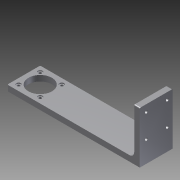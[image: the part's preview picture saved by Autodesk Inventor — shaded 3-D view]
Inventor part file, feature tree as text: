
AUTODESK INVENTOR PART (.ipt)
format: ipt  version: 2011 (Build 150239000, 239)  size: 169,984 bytes
history: native  units: mm
features: extrude x7, sketch x7, fillet x3, projected_geometry x1
ambient origin geometry x8: Origin, YZ Plane, XZ Plane, XY Plane, X Axis, Y Axis, Z Axis, Center Point
bodies: Volumenkörper1 (feature_tree)
feature tree (18):
  extrude  "NEMA11 Halter"  Depth=35.0mm
  extrude  "Motorloch"  Depth=25.0mm
  extrude  "Motorschrauben"  Depth=2.8mm
  extrude  "Extrusion16"  Depth=2.8mm
  extrude  "Extrusion17"  Depth=23.0mm
  extrude  "Extrusion18"  Depth=5.0mm
  fillet  "Rundung8"  Radius=5.0mm
  fillet  "Rundung9"  Radius=5.0mm
  fillet  "Rundung10"  Radius=5.0mm
  extrude  "Extrusion19"  Depth=100.0mm
  sketch  "Skizze1"  dims[d0=35.0mm d1=35.0mm]
  sketch  "Skizze2"  dims[d2=6.0mm d3=0.0mm d4=25.0mm]
  sketch  "Skizze3"  dims[d5=5.0mm d6=0.0mm d7=2.8mm]
  projected_geometry  "Projizierte Kontur1"
  sketch  "Skizze22"  dims[d8=2.8mm d9=23.0mm d10=2.8mm d11=23.0mm]
  sketch  "Skizze23"  dims[d12=2.8mm d13=23.0mm d14=23.0mm]
  sketch  "Skizze24"  dims[d15=5.0mm d16=0.0mm d78=5.0mm d79=5.0mm d80=5.0mm d81=5.0mm]
  sketch  "Skizze25"  dims[d82=1.0mm d83=0.0mm d84=100.0mm d85=6.0mm d86=0.0mm d87=6.0mm d88=55.0mm d89=6.0mm d90=0.0mm d91=5.0mm d92=1.0mm d93=1.0mm d94=3.0mm d95=3.0mm d96=3.0mm d97=3.0mm d98=6.0mm d99=0.0mm]
